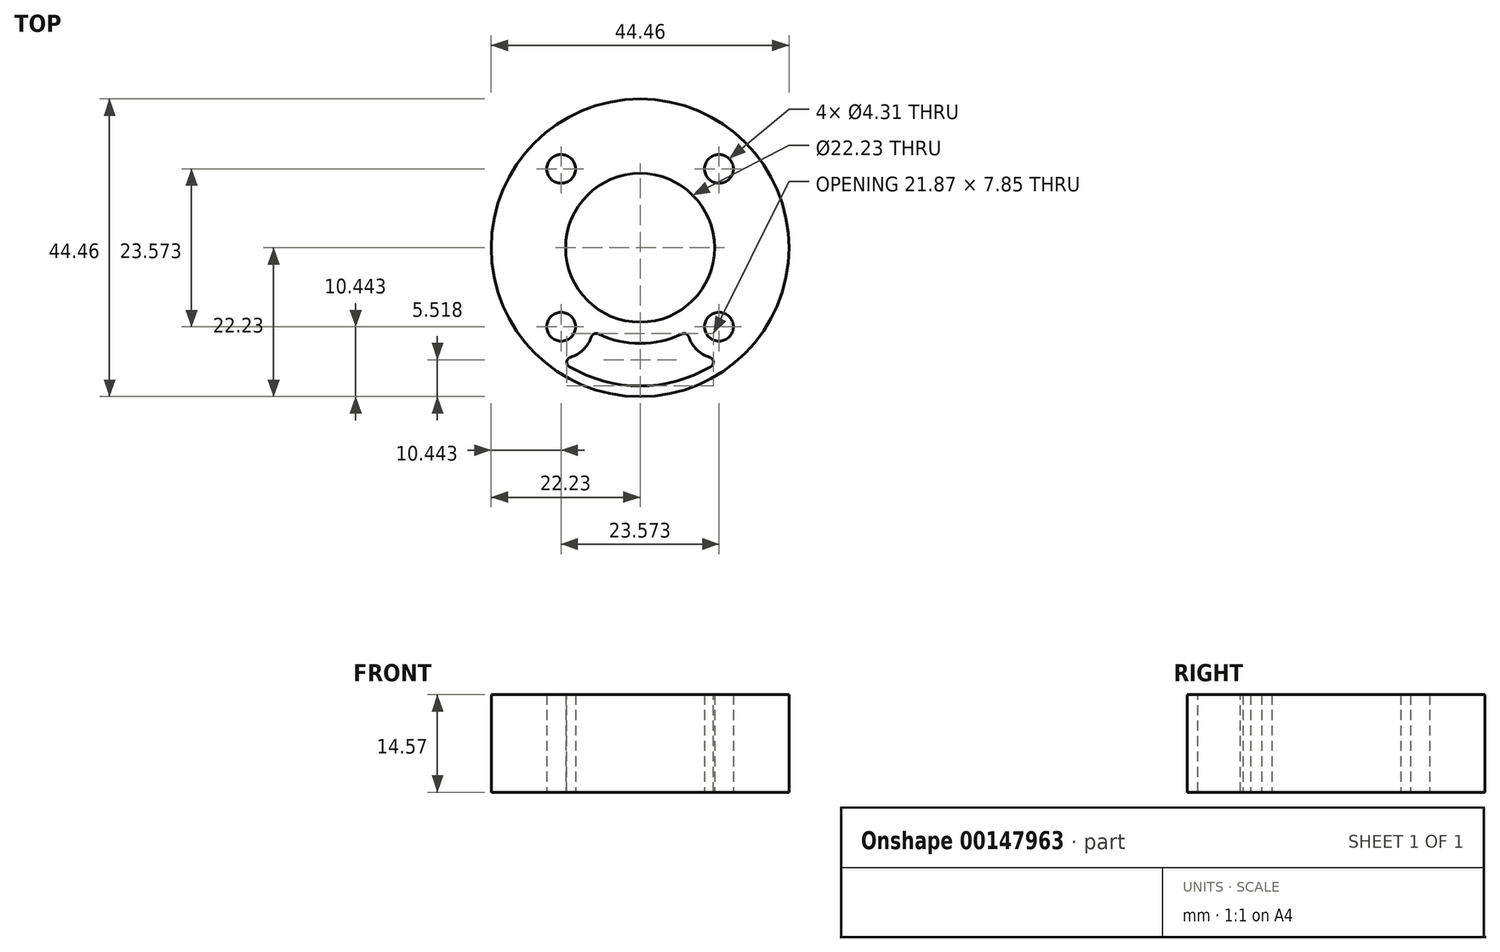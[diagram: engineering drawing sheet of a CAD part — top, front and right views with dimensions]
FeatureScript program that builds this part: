
annotation { "Feature Type Name" : "Feature", "Feature Type Description" : "" }
export const myFeature = defineFeature(function(context is Context, id is Id, definition is map)
    precondition{}
    {
        {
            var Q0;
            Q0=qCreatedBy(makeId("Top.planeOp"),FACE);
            var sketch = newSketch(context, id + "F0", { "sketchPlane" : qUnion([Q0])});
            skCircle(sketch, "E0", {"center": v(0, 0) * mm, "radius": 11.11 * mm});
            skCircle(sketch, "E1", {"center": v(0, 0) * mm, "radius": 22.23 * mm});
            skCircle(sketch, "E2", {"center": v(11.79, 11.79) * mm, "radius": 5.56 * mm, "construction": true});
            skCircle(sketch, "E3", {"center": v(11.79, 11.79) * mm, "radius": 2.15 * mm});
            skCircle(sketch, "E4", {"center": v(11.79, -11.79) * mm, "radius": 2.15 * mm});
            skCircle(sketch, "E5", {"center": v(-11.79, -11.79) * mm, "radius": 2.15 * mm});
            skCircle(sketch, "E6", {"center": v(0, 0) * mm, "radius": 9.53 * mm, "construction": true});
            skLineSegment(sketch, "E7.bottom", {"start": v(11.79, 11.79) * mm, "end": v(-11.79, 11.79) * mm, "construction": true});
            skLineSegment(sketch, "E7.top", {"start": v(11.79, -11.79) * mm, "end": v(-11.79, -11.79) * mm, "construction": true});
            skLineSegment(sketch, "E7.left", {"start": v(11.79, 11.79) * mm, "end": v(11.79, -11.79) * mm, "construction": true});
            skLineSegment(sketch, "E7.right", {"start": v(-11.79, 11.79) * mm, "end": v(-11.79, -11.79) * mm, "construction": true});
            skCircle(sketch, "E8", {"center": v(-11.79, 11.79) * mm, "radius": 2.15 * mm});
            skSolve(sketch);
        }
        {
            var Q0;
            Q0=qSketchRegion(id+"F0",true);
            extrude(context, id + "F1", {"entities" : qUnion([Q0]), "depth" : 14.57 * mm});
        }
        {
            var Q0;
            Q0=makeQuery(id+"F1.opExtrude","CAP_FACE",FACE,{"disambiguationData":[OSD([sQuery(id+"F0.wireOp",EDGE,"E0"),sQuery(id+"F0.wireOp",EDGE,"E1"),sQuery(id+"F0.wireOp",EDGE,"E3"),sQuery(id+"F0.wireOp",EDGE,"E4"),sQuery(id+"F0.wireOp",EDGE,"E5")])],"isStart":false});
            var sketch = newSketch(context, id + "F2", { "sketchPlane" : qUnion([Q0])});
            skArc(sketch, "E9", {"start": v(7.07, -12.42) * mm, "mid": v(8.88, -15.56) * mm, "end": v(12.38, -16.51) * mm});
            skArc(sketch, "E10", {"start": v(-12.38, -16.51) * mm, "mid": v(-8.88, -15.56) * mm, "end": v(-7.07, -12.42) * mm});
            skArc(sketch, "E11", {"start": v(-12.38, -16.51) * mm, "mid": v(0, -20.64) * mm, "end": v(12.38, -16.51) * mm});
            skArc(sketch, "E12", {"start": v(-7.07, -12.42) * mm, "mid": v(0, -14.29) * mm, "end": v(7.07, -12.42) * mm});
            skSolve(sketch);
        }
        {
            var Q0;
            Q0=qSketchRegion(id+"F2",true);
            var Q1;
            Q1=makeQuery(id+"F1.opExtrude","CAP_FACE",FACE,{"disambiguationData":[OSD([sQuery(id+"F0.wireOp",EDGE,"E0"),sQuery(id+"F0.wireOp",EDGE,"E1"),sQuery(id+"F0.wireOp",EDGE,"E3"),sQuery(id+"F0.wireOp",EDGE,"E4"),sQuery(id+"F0.wireOp",EDGE,"E5")])],"isStart":true});
            extrude(context, id + "F3", {"entities" : qUnion([Q0]), "operationType" : NewBodyOperationType.REMOVE, "endBound" : BoundingType.UP_TO_SURFACE, "oppositeDirection" : true, "endBoundEntityFace" : qUnion([Q1]), "depth" : 25.4 * mm});
        }
        {
            var Q0;
            Q0=makeQuery(id+"FdU1y7MwxrunM7S_1.2.F3.boolean.opBoolean","COPY",EDGE,{"derivedFrom":makeQuery(id+"FdU1y7MwxrunM7S_1.2.F3.opExtrude","SWEPT_EDGE",EDGE,{"disambiguationData":[OSD([sQuery(id+"F2.wireOp",EDGE,"E9"),sQuery(id+"F2.wireOp",EDGE,"E11")])]})});
            var Q1;
            Q1=makeQuery(id+"FdU1y7MwxrunM7S_1.2.F3.boolean.opBoolean","COPY",EDGE,{"derivedFrom":makeQuery(id+"FdU1y7MwxrunM7S_1.2.F3.opExtrude","SWEPT_EDGE",EDGE,{"disambiguationData":[OSD([sQuery(id+"F2.wireOp",EDGE,"E9"),sQuery(id+"F2.wireOp",EDGE,"E12")])]})});
            var Q2;
            Q2=makeQuery(id+"FdU1y7MwxrunM7S_1.1.F3.boolean.opBoolean","COPY",EDGE,{"derivedFrom":makeQuery(id+"FdU1y7MwxrunM7S_1.1.F3.opExtrude","SWEPT_EDGE",EDGE,{"disambiguationData":[OSD([sQuery(id+"F2.wireOp",EDGE,"E10"),sQuery(id+"F2.wireOp",EDGE,"E12")])]})});
            var Q3;
            Q3=makeQuery(id+"FdU1y7MwxrunM7S_1.1.F3.boolean.opBoolean","COPY",EDGE,{"derivedFrom":makeQuery(id+"FdU1y7MwxrunM7S_1.1.F3.opExtrude","SWEPT_EDGE",EDGE,{"disambiguationData":[OSD([sQuery(id+"F2.wireOp",EDGE,"E10"),sQuery(id+"F2.wireOp",EDGE,"E11")])]})});
            var Q4;
            Q4=makeQuery(id+"FdU1y7MwxrunM7S_1.2.F3.boolean.opBoolean","COPY",EDGE,{"derivedFrom":makeQuery(id+"FdU1y7MwxrunM7S_1.2.F3.opExtrude","SWEPT_EDGE",EDGE,{"disambiguationData":[OSD([sQuery(id+"F2.wireOp",EDGE,"E10"),sQuery(id+"F2.wireOp",EDGE,"E12")])]})});
            var Q5;
            Q5=makeQuery(id+"FdU1y7MwxrunM7S_1.2.F3.boolean.opBoolean","COPY",EDGE,{"derivedFrom":makeQuery(id+"FdU1y7MwxrunM7S_1.2.F3.opExtrude","SWEPT_EDGE",EDGE,{"disambiguationData":[OSD([sQuery(id+"F2.wireOp",EDGE,"E10"),sQuery(id+"F2.wireOp",EDGE,"E11")])]})});
            var Q6;
            Q6=makeQuery(id+"F3.boolean.opBoolean","COPY",EDGE,{"derivedFrom":makeQuery(id+"F3.opExtrude","SWEPT_EDGE",EDGE,{"disambiguationData":[OSD([sQuery(id+"F2.wireOp",EDGE,"E9"),sQuery(id+"F2.wireOp",EDGE,"E12")])]})});
            var Q7;
            Q7=makeQuery(id+"F3.boolean.opBoolean","COPY",EDGE,{"derivedFrom":makeQuery(id+"F3.opExtrude","SWEPT_EDGE",EDGE,{"disambiguationData":[OSD([sQuery(id+"F2.wireOp",EDGE,"E9"),sQuery(id+"F2.wireOp",EDGE,"E11")])]})});
            var Q8;
            Q8=makeQuery(id+"F3.boolean.opBoolean","COPY",EDGE,{"derivedFrom":makeQuery(id+"F3.opExtrude","SWEPT_EDGE",EDGE,{"disambiguationData":[OSD([sQuery(id+"F2.wireOp",EDGE,"E10"),sQuery(id+"F2.wireOp",EDGE,"E12")])]})});
            var Q9;
            Q9=makeQuery(id+"F3.boolean.opBoolean","COPY",EDGE,{"derivedFrom":makeQuery(id+"F3.opExtrude","SWEPT_EDGE",EDGE,{"disambiguationData":[OSD([sQuery(id+"F2.wireOp",EDGE,"E10"),sQuery(id+"F2.wireOp",EDGE,"E11")])]})});
            var Q10;
            Q10=makeQuery(id+"FdU1y7MwxrunM7S_1.1.F3.boolean.opBoolean","COPY",EDGE,{"derivedFrom":makeQuery(id+"FdU1y7MwxrunM7S_1.1.F3.opExtrude","SWEPT_EDGE",EDGE,{"disambiguationData":[OSD([sQuery(id+"F2.wireOp",EDGE,"E9"),sQuery(id+"F2.wireOp",EDGE,"E11")])]})});
            var Q11;
            Q11=makeQuery(id+"FdU1y7MwxrunM7S_1.1.F3.boolean.opBoolean","COPY",EDGE,{"derivedFrom":makeQuery(id+"FdU1y7MwxrunM7S_1.1.F3.opExtrude","SWEPT_EDGE",EDGE,{"disambiguationData":[OSD([sQuery(id+"F2.wireOp",EDGE,"E9"),sQuery(id+"F2.wireOp",EDGE,"E12")])]})});
            var Q12;
            Q12=makeQuery(id+"FdU1y7MwxrunM7S_1.3.F3.boolean.opBoolean","COPY",EDGE,{"derivedFrom":makeQuery(id+"FdU1y7MwxrunM7S_1.3.F3.opExtrude","SWEPT_EDGE",EDGE,{"disambiguationData":[OSD([sQuery(id+"F2.wireOp",EDGE,"E10"),sQuery(id+"F2.wireOp",EDGE,"E11")])]})});
            var Q13;
            Q13=makeQuery(id+"FdU1y7MwxrunM7S_1.3.F3.boolean.opBoolean","COPY",EDGE,{"derivedFrom":makeQuery(id+"FdU1y7MwxrunM7S_1.3.F3.opExtrude","SWEPT_EDGE",EDGE,{"disambiguationData":[OSD([sQuery(id+"F2.wireOp",EDGE,"E10"),sQuery(id+"F2.wireOp",EDGE,"E12")])]})});
            var Q14;
            Q14=makeQuery(id+"FdU1y7MwxrunM7S_1.3.F3.boolean.opBoolean","COPY",EDGE,{"derivedFrom":makeQuery(id+"FdU1y7MwxrunM7S_1.3.F3.opExtrude","SWEPT_EDGE",EDGE,{"disambiguationData":[OSD([sQuery(id+"F2.wireOp",EDGE,"E9"),sQuery(id+"F2.wireOp",EDGE,"E11")])]})});
            var Q15;
            Q15=makeQuery(id+"FdU1y7MwxrunM7S_1.3.F3.boolean.opBoolean","COPY",EDGE,{"derivedFrom":makeQuery(id+"FdU1y7MwxrunM7S_1.3.F3.opExtrude","SWEPT_EDGE",EDGE,{"disambiguationData":[OSD([sQuery(id+"F2.wireOp",EDGE,"E9"),sQuery(id+"F2.wireOp",EDGE,"E12")])]})});
            fillet(context, id + "F4", {"entities" : qUnion([Q0, Q1, Q2, Q3, Q4, Q5, Q6, Q7, Q8, Q9, Q10, Q11, Q12, Q13, Q14, Q15]), "radius" : 0.76 * mm, "tangentPropagation" : true, "allowEdgeOverflow" : false});
        }
    });
